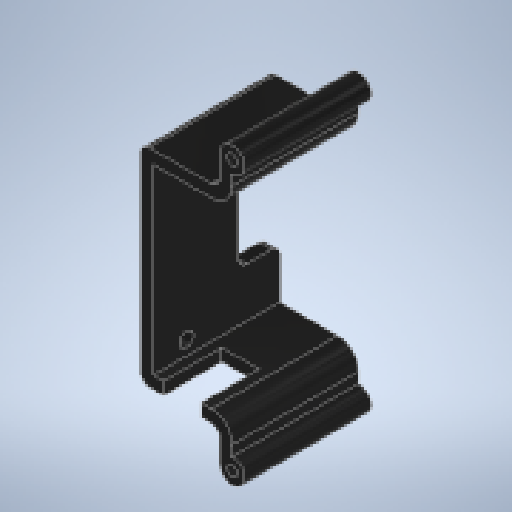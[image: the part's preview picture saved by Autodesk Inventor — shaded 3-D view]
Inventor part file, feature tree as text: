
AUTODESK INVENTOR PART (.ipt)
format: ipt  version: 2025.1 (Build 291241000, 241)  size: 222,720 bytes
history: native  units: mm
features: other x5, sketch x4, extrude x4, reference x3, fillet x1
ambient origin geometry x8: Origin, YZ Plane, XZ Plane, XY Plane, X Axis, Y Axis, Z Axis, Center Point
bodies: Body1 (feature_tree)
feature tree (17):
  other  "ソリッド1"
  sketch  "スケッチ1"
  other  "作業平面1"
  extrude  "押し出し1"  Depth=2.6mm
  extrude  "押し出し2"  Depth=2.6mm
  fillet  "フィレット1"  Radius=6.0mm
  extrude  "押し出し3"  Depth=6.0mm
  extrude  "押し出し4"  Depth=3.0mm
  reference  "参照1"
  reference  "参照2"
  reference  "参照3"
  sketch  "スケッチ2"
  sketch  "スケッチ3"
  sketch  "スケッチ4"
  other  "<userpath>\Documents\Inventor\Vixen\doutai.iam"
  other  "doutai.iam"
  other  "kataue:1"
